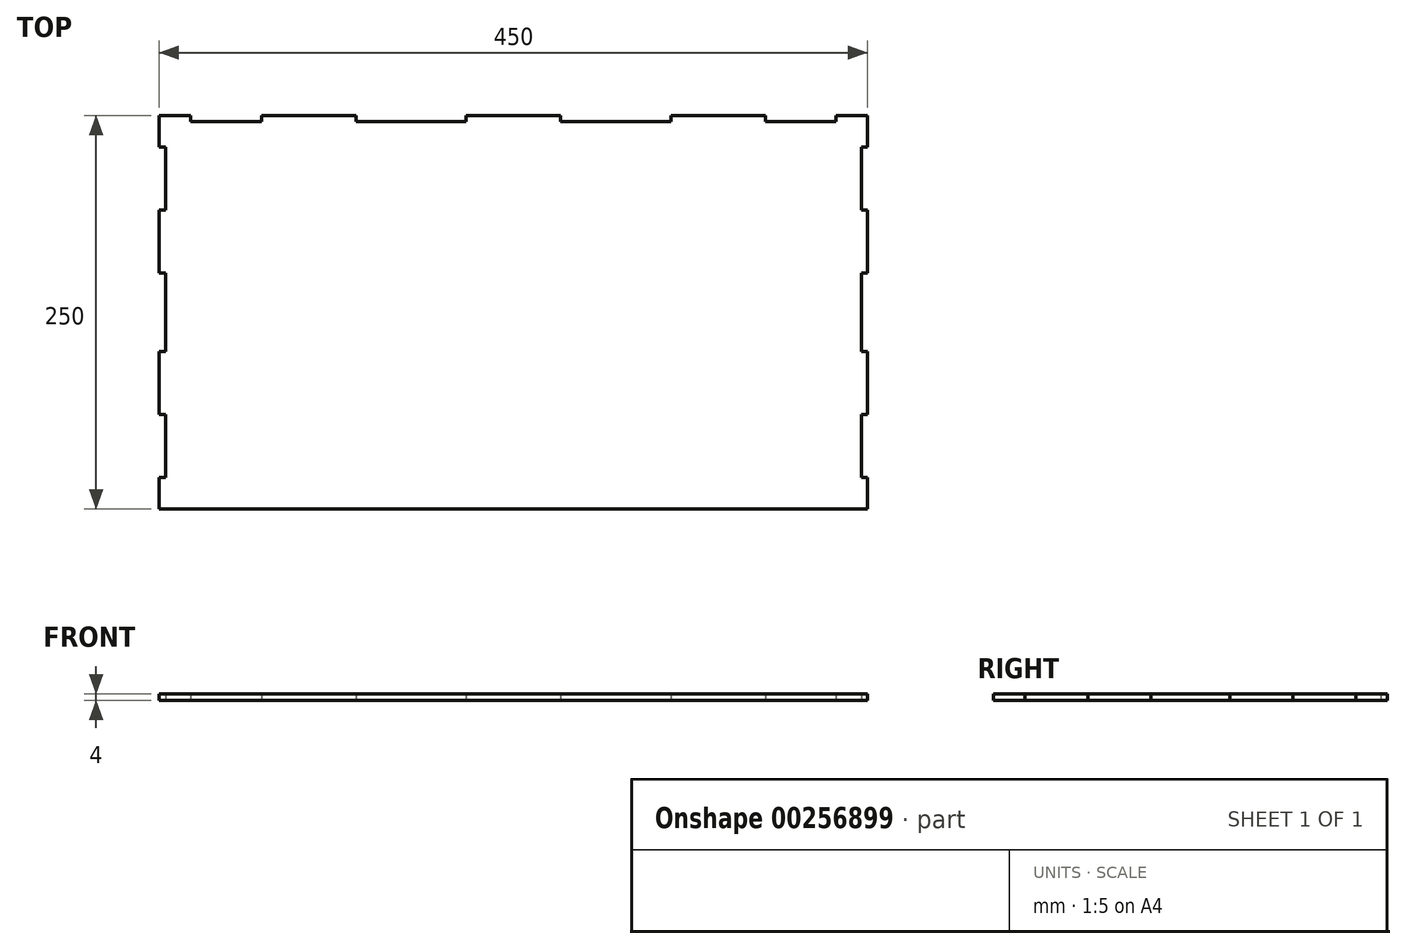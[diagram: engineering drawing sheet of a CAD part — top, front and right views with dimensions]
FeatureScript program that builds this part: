
annotation { "Feature Type Name" : "Feature", "Feature Type Description" : "" }
export const myFeature = defineFeature(function(context is Context, id is Id, definition is map)
    precondition{}
    {
        {
            var Q0;
            Q0=qCreatedBy(makeId("Top.planeOp"),FACE);
            var sketch = newSketch(context, id + "F0", { "sketchPlane" : qUnion([Q0])});
            skLineSegment(sketch, "E0.bottom", {"start": v(0, 0) * mm, "end": v(-450, 0) * mm});
            skLineSegment(sketch, "E0.top", {"start": v(0, 250) * mm, "end": v(-20, 250) * mm});
            skLineSegment(sketch, "E0.right", {"start": v(-450, 0) * mm, "end": v(-450, 20) * mm});
            skLineSegment(sketch, "E1.bottom", {"start": v(-450, 230) * mm, "end": v(-446, 230) * mm});
            skLineSegment(sketch, "E1.top", {"start": v(-450, 190) * mm, "end": v(-446, 190) * mm});
            skLineSegment(sketch, "E1.right", {"start": v(-446, 230) * mm, "end": v(-446, 190) * mm});
            skLineSegment(sketch, "E2.bottom", {"start": v(-450, 20) * mm, "end": v(-446, 20) * mm});
            skLineSegment(sketch, "E2.top", {"start": v(-450, 60) * mm, "end": v(-446, 60) * mm});
            skLineSegment(sketch, "E2.right", {"start": v(-446, 20) * mm, "end": v(-446, 60) * mm});
            skLineSegment(sketch, "E3.bottom", {"start": v(-450, 150) * mm, "end": v(-446, 150) * mm});
            skLineSegment(sketch, "E3.top", {"start": v(-450, 100) * mm, "end": v(-446, 100) * mm});
            skLineSegment(sketch, "E3.right", {"start": v(-446, 150) * mm, "end": v(-446, 100) * mm});
            skLineSegment(sketch, "E4", {"start": v(-450, 230) * mm, "end": v(-450, 250) * mm});
            skLineSegment(sketch, "E5", {"start": v(-450, 150) * mm, "end": v(-450, 190) * mm});
            skLineSegment(sketch, "E6", {"start": v(-450, 100) * mm, "end": v(-450, 100) * mm});
            skLineSegment(sketch, "E7", {"start": v(-450, 60) * mm, "end": v(-450, 100) * mm});
            skLineSegment(sketch, "E8.bottom", {"start": v(0, 230) * mm, "end": v(-4, 230) * mm});
            skLineSegment(sketch, "E8.top", {"start": v(0, 190) * mm, "end": v(-4, 190) * mm});
            skLineSegment(sketch, "E8.right", {"start": v(-4, 230) * mm, "end": v(-4, 190) * mm});
            skLineSegment(sketch, "E9.bottom", {"start": v(0, 150) * mm, "end": v(-4, 150) * mm});
            skLineSegment(sketch, "E9.top", {"start": v(0, 100) * mm, "end": v(-4, 100) * mm});
            skLineSegment(sketch, "E9.right", {"start": v(-4, 150) * mm, "end": v(-4, 100) * mm});
            skLineSegment(sketch, "E10.bottom", {"start": v(0, 60) * mm, "end": v(-4, 60) * mm});
            skLineSegment(sketch, "E10.top", {"start": v(0, 20) * mm, "end": v(-4, 20) * mm});
            skLineSegment(sketch, "E10.right", {"start": v(-4, 60) * mm, "end": v(-4, 20) * mm});
            skLineSegment(sketch, "E11.left", {"start": v(-430, 250) * mm, "end": v(-430, 250) * mm});
            skLineSegment(sketch, "E12", {"start": v(-325, 250) * mm, "end": v(-385, 250) * mm});
            skLineSegment(sketch, "E13", {"start": v(-195, 250) * mm, "end": v(-255, 250) * mm});
            skLineSegment(sketch, "E14", {"start": v(-65, 250) * mm, "end": v(-125, 250) * mm});
            skLineSegment(sketch, "E15", {"start": v(-430, 250) * mm, "end": v(-450, 250) * mm});
            skLineSegment(sketch, "E16", {"start": v(0, 0) * mm, "end": v(0, 20) * mm});
            skLineSegment(sketch, "E17", {"start": v(0, 60) * mm, "end": v(0, 100) * mm});
            skLineSegment(sketch, "E18", {"start": v(0, 190) * mm, "end": v(0, 150) * mm});
            skLineSegment(sketch, "E19", {"start": v(0, 230) * mm, "end": v(0, 250) * mm});
            skLineSegment(sketch, "E20", {"start": v(-195, 250) * mm, "end": v(-195, 246) * mm});
            skLineSegment(sketch, "E21", {"start": v(-195, 246) * mm, "end": v(-125, 246) * mm});
            skLineSegment(sketch, "E22", {"start": v(-125, 246) * mm, "end": v(-125, 250) * mm});
            skLineSegment(sketch, "E23", {"start": v(-65, 246) * mm, "end": v(-20, 246) * mm});
            skLineSegment(sketch, "E24", {"start": v(-20, 246) * mm, "end": v(-20, 250) * mm});
            skLineSegment(sketch, "E25", {"start": v(-65, 250) * mm, "end": v(-65, 246) * mm});
            skLineSegment(sketch, "E26", {"start": v(-255, 250) * mm, "end": v(-255, 246) * mm});
            skLineSegment(sketch, "E27", {"start": v(-255, 246) * mm, "end": v(-325, 246) * mm});
            skLineSegment(sketch, "E28", {"start": v(-325, 246) * mm, "end": v(-325, 250) * mm});
            skLineSegment(sketch, "E29", {"start": v(-385, 250) * mm, "end": v(-385, 246) * mm});
            skLineSegment(sketch, "E30", {"start": v(-385, 246) * mm, "end": v(-430, 246) * mm});
            skLineSegment(sketch, "E31", {"start": v(-430, 246) * mm, "end": v(-430, 250) * mm});
            skSolve(sketch);
        }
        {
            var Q0;
            Q0=makeQuery(id+"F0.imprint","IMPRINT",FACE,{"disambiguationData":[TD([[makeQuery(id+"F0.imprint","IMPRINT",EDGE,{"derivedFrom":sQuery(id+"F0.wireOp",EDGE,"E0.bottom")}),-1.0]])]});
            extrude(context, id + "F1", {"entities" : qUnion([Q0]), "depth" : 4 * mm});
        }
    });
